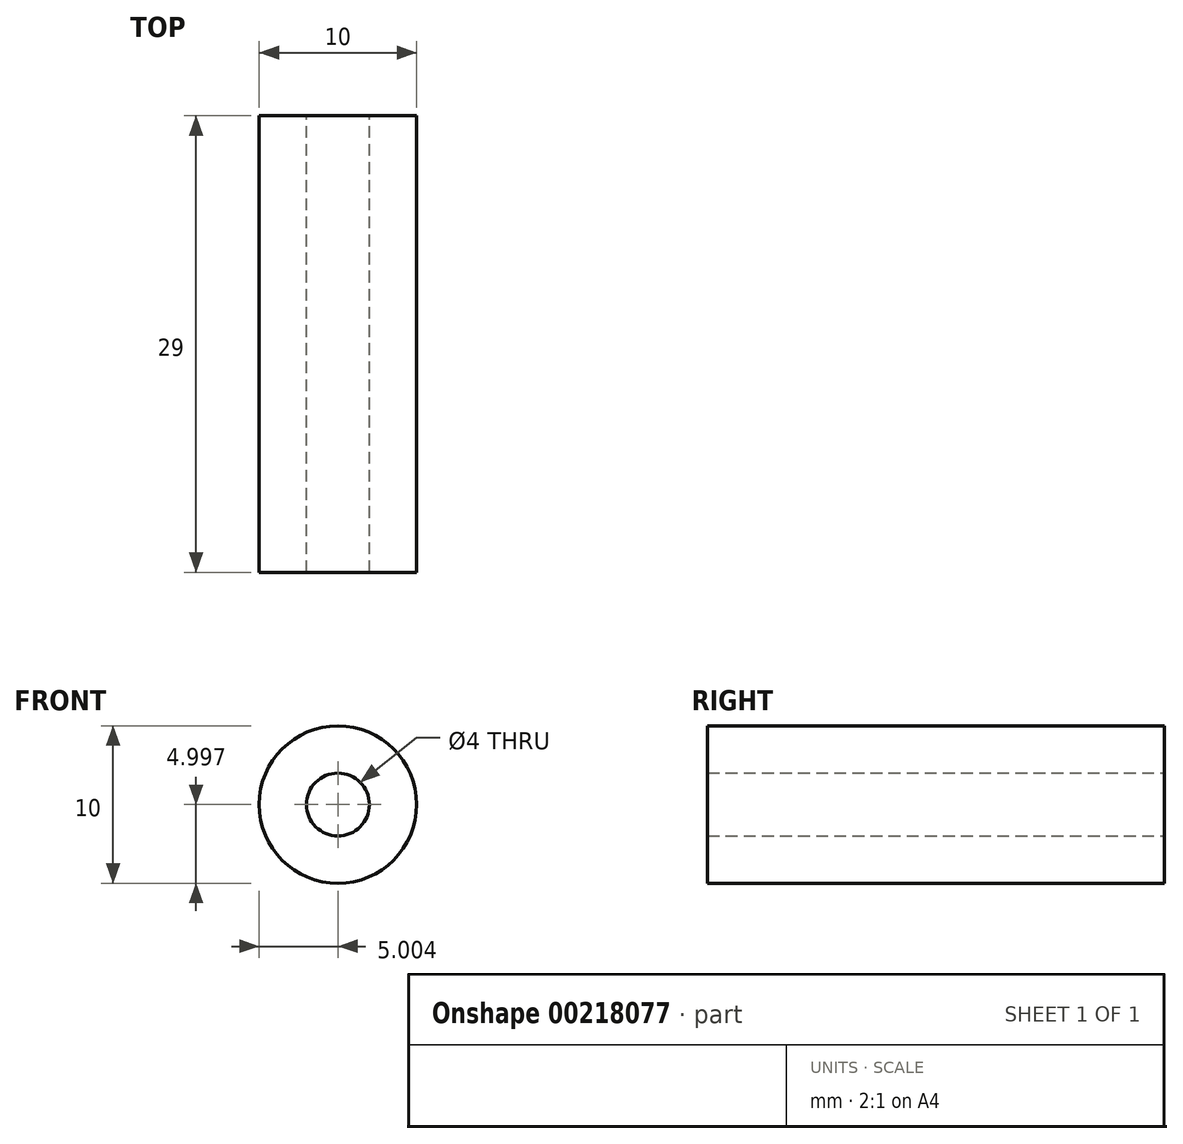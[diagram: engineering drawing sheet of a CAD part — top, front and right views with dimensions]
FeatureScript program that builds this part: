
annotation { "Feature Type Name" : "Feature", "Feature Type Description" : "" }
export const myFeature = defineFeature(function(context is Context, id is Id, definition is map)
    precondition{}
    {
        {
            var Q0;
            Q0=qCreatedBy(makeId("Front.planeOp"),FACE);
            var sketch = newSketch(context, id + "F0", { "sketchPlane" : qUnion([Q0])});
            skCircle(sketch, "E0", {"center": v(-21.55, 24.77) * mm, "radius": 5 * mm});
            skCircle(sketch, "E1", {"center": v(-21.55, 24.77) * mm, "radius": 2 * mm});
            skSolve(sketch);
        }
        {
            var Q0;
            Q0=makeQuery(id+"F0.imprint","IMPRINT",FACE,{"disambiguationData":[TD([[makeQuery(id+"F0.imprint","IMPRINT",EDGE,{"derivedFrom":sQuery(id+"F0.wireOp",EDGE,"E0")}),1.0]])]});
            extrude(context, id + "F1", {"entities" : qUnion([Q0]), "depth" : 29 * mm});
        }
        {
            var Q0;
            Q0=makeQuery(id+"F0.imprint","IMPRINT",FACE,{"disambiguationData":[TD([[makeQuery(id+"F0.imprint","IMPRINT",EDGE,{"derivedFrom":sQuery(id+"F0.wireOp",EDGE,"E1")}),1.0]])]});
            extrude(context, id + "F2", {"entities" : qUnion([Q0]), "oppositeDirection" : true, "depth" : 4 * mm});
        }
        {
            var Q0;
            Q0=makeQuery(id+"F2.opExtrude","SWEPT_BODY",BODY,{"disambiguationData":[OSD([sQuery(id+"F0.wireOp",EDGE,"E1")])]});
            deleteBodies(context, id + "F3", {"entities" : qUnion([Q0])});
        }
    });
